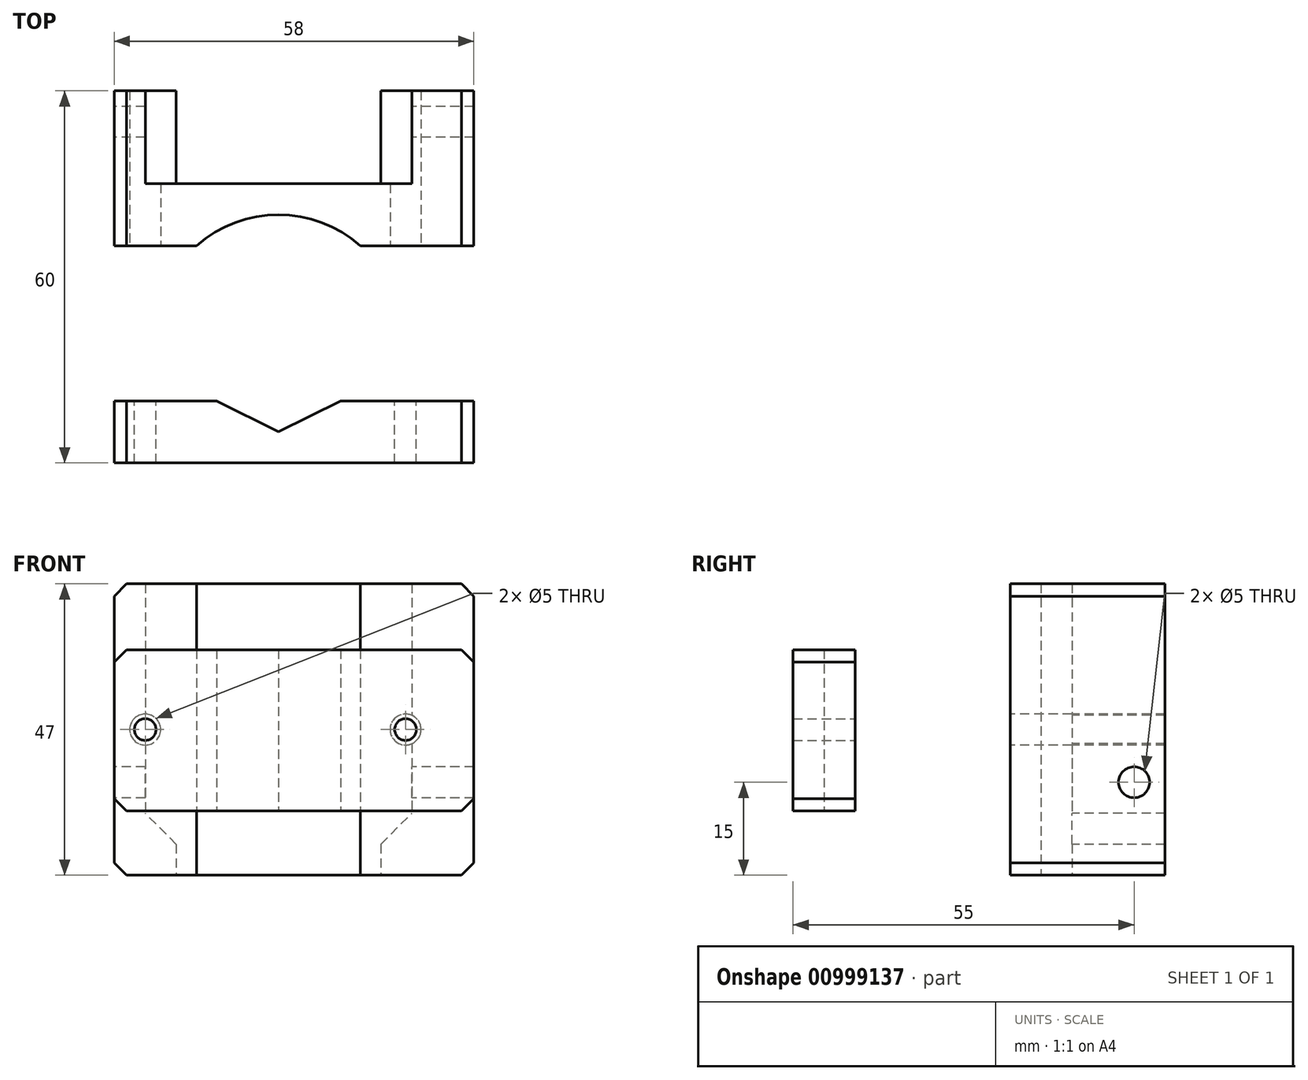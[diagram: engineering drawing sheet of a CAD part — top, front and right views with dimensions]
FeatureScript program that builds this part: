
annotation { "Feature Type Name" : "Feature", "Feature Type Description" : "" }
export const myFeature = defineFeature(function(context is Context, id is Id, definition is map)
    precondition{}
    {
        {
            var Q0;
            Q0=qCreatedBy(makeId("Top.planeOp"),FACE);
            var sketch = newSketch(context, id + "F0", { "sketchPlane" : qUnion([Q0])});
            skLineSegment(sketch, "E0.bottom", {"start": v(-26.5, 10) * mm, "end": v(-21.5, 10) * mm});
            skLineSegment(sketch, "E0.left", {"start": v(-26.5, 10) * mm, "end": v(-26.5, -10) * mm});
            skLineSegment(sketch, "E0.right", {"start": v(31.5, 10) * mm, "end": v(31.5, -10) * mm});
            skLineSegment(sketch, "E1.top", {"start": v(-21.5, -5) * mm, "end": v(21.5, -5) * mm});
            skLineSegment(sketch, "E1.left", {"start": v(-21.5, 10) * mm, "end": v(-21.5, -5) * mm});
            skLineSegment(sketch, "E1.right", {"start": v(21.5, 10) * mm, "end": v(21.5, -5) * mm});
            skLineSegment(sketch, "E2.top", {"start": v(-26.5, -15) * mm, "end": v(-13.23, -15) * mm});
            skLineSegment(sketch, "E2.left", {"start": v(-26.5, -10) * mm, "end": v(-26.5, -15) * mm});
            skLineSegment(sketch, "E2.right", {"start": v(31.5, -10) * mm, "end": v(31.5, -15) * mm});
            skArc(sketch, "E3", {"start": v(13.23, -15) * mm, "mid": v(0, -10) * mm, "end": v(-13.23, -15) * mm});
            skLineSegment(sketch, "E4.trimOffspring", {"start": v(13.23, -15) * mm, "end": v(31.5, -15) * mm});
            skLineSegment(sketch, "E5.trimOffspring", {"start": v(21.5, 10) * mm, "end": v(31.5, 10) * mm});
            skLineSegment(sketch, "E6.bottom", {"start": v(-21.5, 10) * mm, "end": v(-16.5, 10) * mm});
            skLineSegment(sketch, "E6.top", {"start": v(-21.5, -5) * mm, "end": v(-16.5, -5) * mm});
            skLineSegment(sketch, "E6.right", {"start": v(-16.5, 10) * mm, "end": v(-16.5, -5) * mm});
            skLineSegment(sketch, "E7.bottom", {"start": v(21.5, 10) * mm, "end": v(16.5, 10) * mm});
            skLineSegment(sketch, "E7.top", {"start": v(21.5, -5) * mm, "end": v(16.5, -5) * mm});
            skLineSegment(sketch, "E7.right", {"start": v(16.5, 10) * mm, "end": v(16.5, -5) * mm});
            skSolve(sketch);
        }
        {
            var Q0;
            Q0=makeQuery(id+"F0.imprint","IMPRINT",FACE,{"disambiguationData":[TD([[makeQuery(id+"F0.imprint","IMPRINT",EDGE,{"derivedFrom":sQuery(id+"F0.wireOp",EDGE,"E0.bottom")}),-1.0]])]});
            extrude(context, id + "F1", {"entities" : qUnion([Q0]), "depth" : 47 * mm, "offsetDistance" : 25 * mm});
        }
        {
            var Q0;
            {var subQ2=sQuery(id+"F0.wireOp",EDGE,"E1.left");Q0=makeQuery(id+"F0.imprint","IMPRINT",FACE,{"disambiguationData":[TD([[makeQuery(id+"F0.imprint","IMPRINT",EDGE,{"derivedFrom":subQ2}),1.0]])]});}
            var Q1;
            {var subQ0=sQuery(id+"F0.wireOp",EDGE,"E1.right");Q1=makeQuery(id+"F0.imprint","IMPRINT",FACE,{"disambiguationData":[TD([[makeQuery(id+"F0.imprint","IMPRINT",EDGE,{"derivedFrom":subQ0}),-1.0]])]});}
            extrude(context, id + "F2", {"entities" : qUnion([Q0, Q1]), "operationType" : NewBodyOperationType.ADD, "depth" : 5 * mm, "offsetDistance" : 25 * mm});
        }
        {
            var Q0;
            Q0=makeQuery(id+"F1.opExtrude","SWEPT_FACE",FACE,{"disambiguationData":[OSD([sQuery(id+"F0.wireOp",EDGE,"E0.left"),sQuery(id+"F0.wireOp",EDGE,"E2.left")])]});
            var sketch = newSketch(context, id + "F3", { "sketchPlane" : qUnion([Q0])});
            skCircle(sketch, "E8", {"center": v(-5, 15) * mm, "radius": 2.5 * mm});
            skPoint(sketch, "E8.centerSnap0", {"position": v(-10, 15) * mm});
            skSolve(sketch);
        }
        {
            var Q0;
            Q0=makeQuery(id+"F3.imprint","IMPRINT",FACE,{"disambiguationData":[TD([[makeQuery(id+"F3.imprint","IMPRINT",EDGE,{"derivedFrom":sQuery(id+"F3.wireOp",EDGE,"E8")}),1.0]])]});
            extrude(context, id + "F4", {"entities" : qUnion([Q0]), "operationType" : NewBodyOperationType.REMOVE, "oppositeDirection" : true, "depth" : 60 * mm, "offsetDistance" : 25 * mm});
        }
        {
            var Q0;
            Q0=makeQuery(id+"F1.opExtrude","SWEPT_FACE",FACE,{"disambiguationData":[OSD([sQuery(id+"F0.wireOp",EDGE,"E4.trimOffspring")])]});
            var sketch = newSketch(context, id + "F5", { "sketchPlane" : qUnion([Q0])});
            skCircle(sketch, "E9", {"center": v(20.5, 23.5) * mm, "radius": 2.5 * mm});
            skPoint(sketch, "E9.centerSnap0", {"position": v(31.5, 23.5) * mm});
            skCircle(sketch, "E10", {"center": v(-21.5, 23.5) * mm, "radius": 2.5 * mm});
            skSolve(sketch);
        }
        {
            var Q0;
            Q0=makeQuery(id+"F5.imprint","IMPRINT",FACE,{"disambiguationData":[TD([[makeQuery(id+"F5.imprint","IMPRINT",EDGE,{"derivedFrom":sQuery(id+"F5.wireOp",EDGE,"E9")}),1.0]])]});
            var Q1;
            Q1=makeQuery(id+"F5.imprint","IMPRINT",FACE,{"disambiguationData":[TD([[makeQuery(id+"F5.imprint","IMPRINT",EDGE,{"derivedFrom":sQuery(id+"F5.wireOp",EDGE,"E10")}),1.0]])]});
            extrude(context, id + "F6", {"entities" : qUnion([Q0, Q1]), "operationType" : NewBodyOperationType.REMOVE, "oppositeDirection" : true, "depth" : 60 * mm, "offsetDistance" : 25 * mm});
        }
        {
            var Q0;
            Q0=makeQuery(id+"F1.opExtrude","SWEPT_FACE",FACE,{"disambiguationData":[OSD([sQuery(id+"F0.wireOp",EDGE,"E1.top")])]});
            var sketch = newSketch(context, id + "F7", { "sketchPlane" : qUnion([Q0])});
            skLineSegment(sketch, "E11", {"start": v(21.5, 5) * mm, "end": v(16.5, 5) * mm});
            skLineSegment(sketch, "E12", {"start": v(16.5, 5) * mm, "end": v(21.5, 10) * mm});
            skLineSegment(sketch, "E13", {"start": v(21.5, 10) * mm, "end": v(21.5, 5) * mm});
            skLineSegment(sketch, "E14.MirrorCS", {"start": v(-16.5, 5) * mm, "end": v(-21.5, 10) * mm});
            skLineSegment(sketch, "E15.MirrorCS", {"start": v(-21.5, 5) * mm, "end": v(-16.5, 5) * mm});
            skLineSegment(sketch, "E16.MirrorCS", {"start": v(-21.5, 10) * mm, "end": v(-21.5, 5) * mm});
            skSolve(sketch);
        }
        {
            var Q0;
            Q0=makeQuery(id+"F7.imprint","IMPRINT",FACE,{"disambiguationData":[TD([[makeQuery(id+"F7.imprint","IMPRINT",EDGE,{"derivedFrom":sQuery(id+"F7.wireOp",EDGE,"E11")}),-1.0]])]});
            var Q1;
            Q1=makeQuery(id+"F7.imprint","IMPRINT",FACE,{"disambiguationData":[TD([[makeQuery(id+"F7.imprint","IMPRINT",EDGE,{"derivedFrom":sQuery(id+"F7.wireOp",EDGE,"E14.MirrorCS")}),1.0]])]});
            extrude(context, id + "F8", {"entities" : qUnion([Q0, Q1]), "operationType" : NewBodyOperationType.ADD, "depth" : 15 * mm, "offsetDistance" : 25 * mm});
        }
        {
            var Q0;
            Q0=makeQuery(id+"F1.opExtrude","CAP_EDGE",EDGE,{"disambiguationData":[OSD([sQuery(id+"F0.wireOp",EDGE,"E0.right"),sQuery(id+"F0.wireOp",EDGE,"E2.right")])],"isStart":true});
            var Q1;
            Q1=makeQuery(id+"F1.opExtrude","CAP_EDGE",EDGE,{"disambiguationData":[OSD([sQuery(id+"F0.wireOp",EDGE,"E0.left"),sQuery(id+"F0.wireOp",EDGE,"E2.left")])],"isStart":true});
            var Q2;
            Q2=makeQuery(id+"F1.opExtrude","CAP_EDGE",EDGE,{"disambiguationData":[OSD([sQuery(id+"F0.wireOp",EDGE,"E0.left"),sQuery(id+"F0.wireOp",EDGE,"E2.left")])],"isStart":false});
            var Q3;
            Q3=makeQuery(id+"F1.opExtrude","CAP_EDGE",EDGE,{"disambiguationData":[OSD([sQuery(id+"F0.wireOp",EDGE,"E0.right"),sQuery(id+"F0.wireOp",EDGE,"E2.right")])],"isStart":false});
            chamfer(context, id + "F9", {"entities" : qUnion([Q0, Q1, Q2, Q3]), "width" : 2 * mm, "tangentPropagation" : true});
        }
        {
            var Q0;
            Q0=makeQuery(id+"F1.opExtrude","SWEPT_FACE",FACE,{"disambiguationData":[OSD([sQuery(id+"F0.wireOp",EDGE,"E2.top")])]});
            cPlane(context, id + "F10", {"entities" : qUnion([Q0]), "cplaneType" : CPlaneType.OFFSET, "offset" : 25 * mm, "width" : 150 * mm, "height" : 150 * mm});
        }
        {
            var Q0;
            Q0=qCreatedBy(id+"F10.planeOp",FACE);
            var sketch = newSketch(context, id + "F11", { "sketchPlane" : qUnion([Q0])});
            skLineSegment(sketch, "E17.0", {"start": v(31.5, 45) * mm, "end": v(31.5, 2) * mm});
            skLineSegment(sketch, "E18.0.0", {"start": v(-13.23, 47) * mm, "end": v(-24.5, 47) * mm});
            skLineSegment(sketch, "E18.0.1", {"start": v(-24.5, 47) * mm, "end": v(-26.5, 45) * mm});
            skLineSegment(sketch, "E18.0.2", {"start": v(-26.5, 45) * mm, "end": v(-26.5, 2) * mm});
            skLineSegment(sketch, "E18.0.3", {"start": v(-26.5, 2) * mm, "end": v(-24.5, 0) * mm});
            skLineSegment(sketch, "E18.0.4", {"start": v(-24.5, 0) * mm, "end": v(-13.23, 0) * mm});
            skLineSegment(sketch, "E18.0.5", {"start": v(-13.23, 0) * mm, "end": v(-13.23, 47) * mm});
            skLineSegment(sketch, "E19.0.0", {"start": v(31.5, 2) * mm, "end": v(31.5, 45) * mm});
            skLineSegment(sketch, "E19.0.1", {"start": v(31.5, 45) * mm, "end": v(29.5, 47) * mm});
            skLineSegment(sketch, "E19.0.2", {"start": v(29.5, 47) * mm, "end": v(13.23, 47) * mm});
            skLineSegment(sketch, "E19.0.3", {"start": v(13.23, 47) * mm, "end": v(13.23, 0) * mm});
            skLineSegment(sketch, "E19.0.4", {"start": v(13.23, 0) * mm, "end": v(29.5, 0) * mm});
            skLineSegment(sketch, "E19.0.5", {"start": v(29.5, 0) * mm, "end": v(31.5, 2) * mm});
            skLineSegment(sketch, "E20.bottom", {"start": v(-26.5, 10.36) * mm, "end": v(31.5, 10.36) * mm});
            skLineSegment(sketch, "E20.top", {"start": v(-26.5, 36.36) * mm, "end": v(31.5, 36.36) * mm});
            skLineSegment(sketch, "E20.left", {"start": v(-26.5, 10.36) * mm, "end": v(-26.5, 36.36) * mm});
            skLineSegment(sketch, "E20.right", {"start": v(31.5, 10.36) * mm, "end": v(31.5, 36.36) * mm});
            skCircle(sketch, "E21.0", {"center": v(20.5, 23.5) * mm, "radius": 2.5 * mm});
            skCircle(sketch, "E22.0", {"center": v(-21.5, 23.5) * mm, "radius": 2.5 * mm});
            skCircle(sketch, "E23", {"center": v(20.5, 23.5) * mm, "radius": 1.75 * mm});
            skCircle(sketch, "E24", {"center": v(-21.5, 23.5) * mm, "radius": 1.75 * mm});
            skSolve(sketch);
        }
        {
            var Q0;
            Q0=makeQuery(id+"F11.imprint","IMPRINT",FACE,{"disambiguationData":[TD([[makeQuery(id+"F11.imprint","IMPRINT",EDGE,{"derivedFrom":sQuery(id+"F11.wireOp",EDGE,"E21.0")}),-1.0]])]});
            var Q1;
            {var subQ0=sQuery(id+"F11.wireOp",EDGE,"E20.bottom");var subQ1=sQuery(id+"F11.wireOp",EDGE,"E18.0.5");var subQ2=makeQuery(id+"F11.imprint","INTERSECT",VERTEX,{"derivedFrom":[subQ1,subQ0]});Q1=makeQuery(id+"F11.imprint","IMPRINT",FACE,{"disambiguationData":[TD([[makeQuery(id+"F11.imprint","IMPRINT",EDGE,{"disambiguationData":[TD([[subQ2,-1.0]])],"derivedFrom":subQ1}),-1.0]])]});}
            var Q2;
            Q2=makeQuery(id+"F11.imprint","IMPRINT",FACE,{"disambiguationData":[TD([[makeQuery(id+"F11.imprint","IMPRINT",EDGE,{"derivedFrom":sQuery(id+"F11.wireOp",EDGE,"E22.0")}),-1.0]])]});
            var Q3;
            Q3=makeQuery(id+"F11.imprint","IMPRINT",FACE,{"disambiguationData":[TD([[makeQuery(id+"F11.imprint","IMPRINT",EDGE,{"derivedFrom":sQuery(id+"F11.wireOp",EDGE,"E21.0")}),1.0]])]});
            var Q4;
            Q4=makeQuery(id+"F11.imprint","IMPRINT",FACE,{"disambiguationData":[TD([[makeQuery(id+"F11.imprint","IMPRINT",EDGE,{"derivedFrom":sQuery(id+"F11.wireOp",EDGE,"E22.0")}),1.0]])]});
            extrude(context, id + "F12", {"entities" : qUnion([Q0, Q1, Q2, Q3, Q4]), "depth" : 10 * mm, "offsetDistance" : 25 * mm});
        }
        {
            var Q0;
            Q0=makeQuery(id+"F12.opExtrude","SWEPT_EDGE",EDGE,{"disambiguationData":[OSD([sQuery(id+"F11.wireOp",EDGE,"E18.0.2"),sQuery(id+"F11.wireOp",EDGE,"E20.bottom")])]});
            var Q1;
            Q1=makeQuery(id+"F12.opExtrude","SWEPT_EDGE",EDGE,{"disambiguationData":[OSD([sQuery(id+"F11.wireOp",EDGE,"E18.0.2"),sQuery(id+"F11.wireOp",EDGE,"E20.top")])]});
            var Q2;
            Q2=makeQuery(id+"F12.opExtrude","SWEPT_EDGE",EDGE,{"disambiguationData":[OSD([sQuery(id+"F11.wireOp",EDGE,"E17.0"),sQuery(id+"F11.wireOp",EDGE,"E20.top")])]});
            var Q3;
            Q3=makeQuery(id+"F12.opExtrude","SWEPT_EDGE",EDGE,{"disambiguationData":[OSD([sQuery(id+"F11.wireOp",EDGE,"E17.0"),sQuery(id+"F11.wireOp",EDGE,"E20.bottom")])]});
            chamfer(context, id + "F13", {"entities" : qUnion([Q0, Q1, Q2, Q3]), "width" : 2 * mm, "tangentPropagation" : true});
        }
        {
            var Q0;
            Q0=makeQuery(id+"F12.opExtrude","SWEPT_FACE",FACE,{"disambiguationData":[OSD([sQuery(id+"F11.wireOp",EDGE,"E20.bottom")])]});
            var sketch = newSketch(context, id + "F14", { "sketchPlane" : qUnion([Q0])});
            skLineSegment(sketch, "E25", {"start": v(0, 45) * mm, "end": v(-10, 40) * mm});
            skLineSegment(sketch, "E26", {"start": v(-10, 40) * mm, "end": v(10, 40) * mm});
            skLineSegment(sketch, "E27", {"start": v(10, 40) * mm, "end": v(0, 45) * mm});
            skSolve(sketch);
        }
        {
            var Q0;
            Q0=makeQuery(id+"F14.imprint","IMPRINT",FACE,{"disambiguationData":[TD([[makeQuery(id+"F14.imprint","IMPRINT",EDGE,{"derivedFrom":sQuery(id+"F14.wireOp",EDGE,"E25")}),1.0]])]});
            extrude(context, id + "F15", {"entities" : qUnion([Q0]), "operationType" : NewBodyOperationType.REMOVE, "oppositeDirection" : true, "depth" : 40 * mm, "offsetDistance" : 25 * mm});
        }
    });
